SOLIDWORKS PART (.sldprt)
format: sldprt  version: not decoded by parser v0  size: 138,752 bytes
history: native  units: mm
features: sketch x4, plane x3, extrude x2, cut_extrude x2, material x1 (+8 scaffold rows collapsed)
feature tree (20):
  scaffold x8  (default folders/planes/origin — collapsed)
  material  "Matériau <non spécifié>"
  plane  "Plan de face"
  plane  "Plan de dessus"
  plane  "Plan de droite"
  sketch  "Esquisse1"  dims[D1=1.75mm D2=3.0mm D3=5.05mm D4=5.05mm D5=2.8mm D6=2.8mm]
  extrude  "Extrusion1"  Depth=10mm
  sketch  "Esquisse2"  dims[D1=~0.368046mm]
  cut_extrude  "Enlèv. mat.-Extru.1"  [1 undecoded]
  sketch  "Esquisse3"  dims[D3=0.3mm D1=1.4mm D2=1.16mm]
  cut_extrude  "Enlèv. mat.-Extru.2"  Depth=2.5mm
  sketch  "Esquisse5"  dims[D1=~0.391737mm]
  extrude  "Extrusion2"  Depth=3mm
decode coverage: 7 of 8 modeling features carry decoded parameters
note: ~ marks probable driven/reference dimensions
note: 1 parameter value undecoded
note: suppression state not decoded; provenance and decode notes live in map.json
